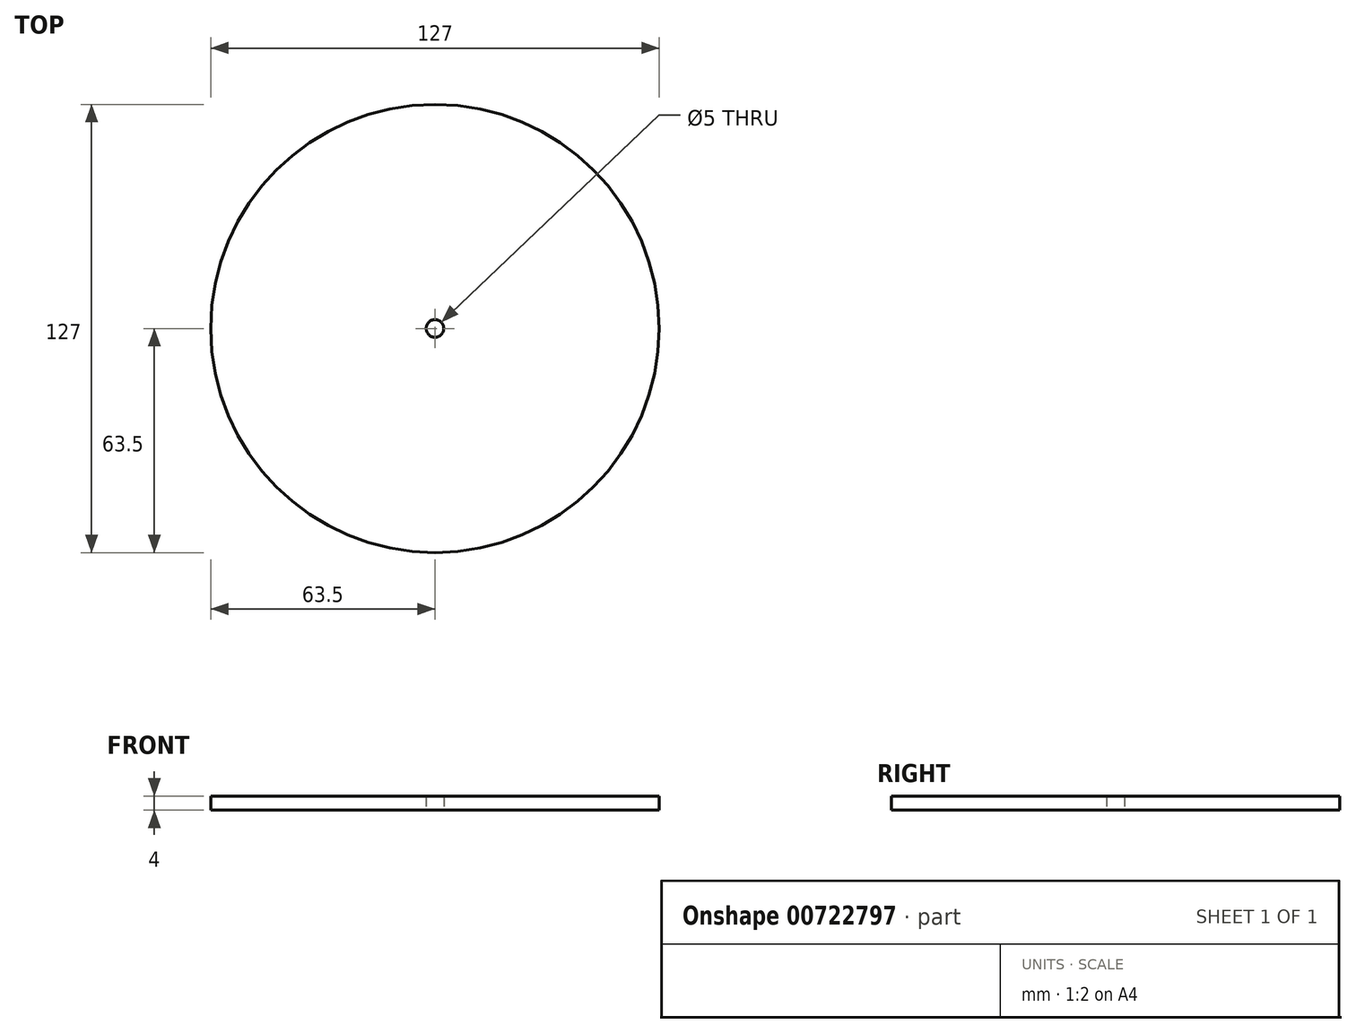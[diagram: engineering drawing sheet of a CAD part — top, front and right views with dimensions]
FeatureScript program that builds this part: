
annotation { "Feature Type Name" : "Feature", "Feature Type Description" : "" }
export const myFeature = defineFeature(function(context is Context, id is Id, definition is map)
    precondition{}
    {
        {
            var Q0;
            Q0=qCreatedBy(makeId("Top.planeOp"),FACE);
            var sketch = newSketch(context, id + "F0", { "sketchPlane" : qUnion([Q0])});
            skCircle(sketch, "E0", {"center": v(0, 0) * mm, "radius": 63.5 * mm});
            skCircle(sketch, "E1", {"center": v(0, 0) * mm, "radius": 2.5 * mm});
            skSolve(sketch);
        }
        {
            var Q0;
            Q0 = qSketchRegion(id + "F0", true);
            extrude(context, id + "F1", {"entities" : qUnion([Q0]), "depth" : 4 * mm, "offsetDistance" : 25 * mm});
        }
    });
